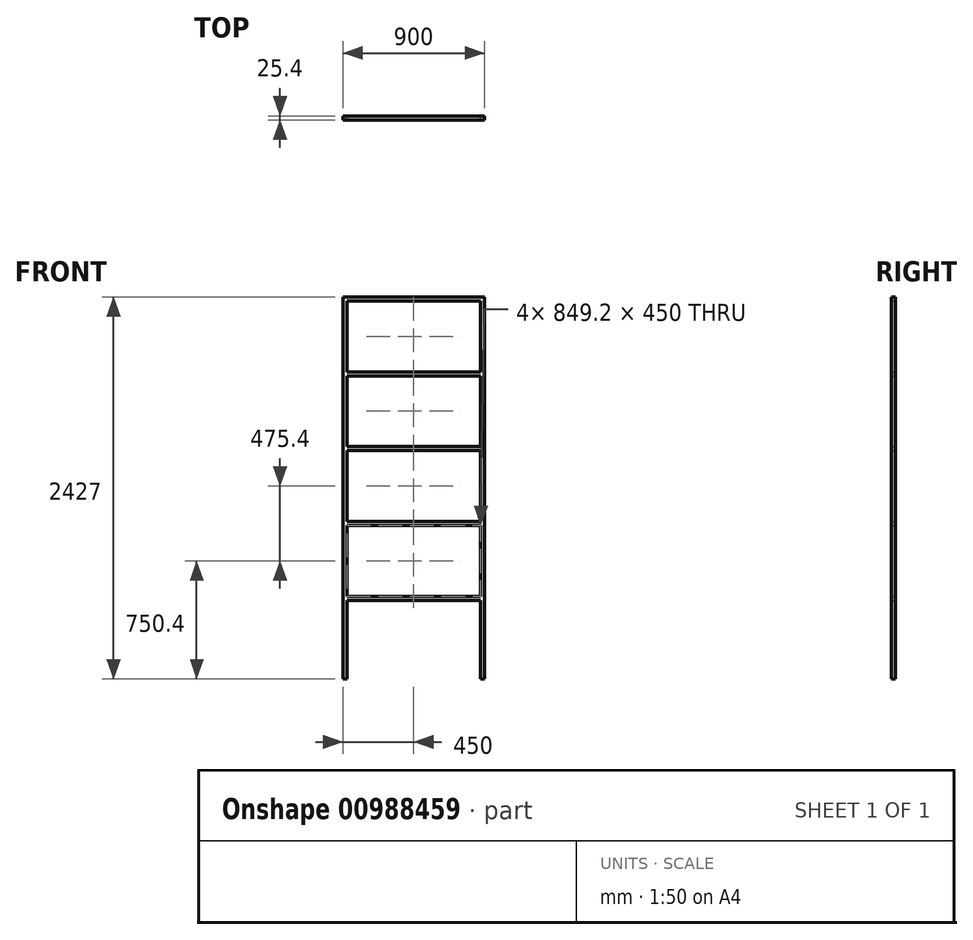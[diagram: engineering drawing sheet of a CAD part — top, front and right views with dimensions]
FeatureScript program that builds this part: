
annotation { "Feature Type Name" : "Feature", "Feature Type Description" : "" }
export const myFeature = defineFeature(function(context is Context, id is Id, definition is map)
    precondition{}
    {
        {
            var Q0;
            Q0=qCreatedBy(makeId("Front.planeOp"),FACE);
            var sketch = newSketch(context, id + "F0", { "sketchPlane" : qUnion([Q0])});
            skLineSegment(sketch, "E0", {"start": v(0, 0) * mm, "end": v(25.4, 0) * mm});
            skLineSegment(sketch, "E1", {"start": v(25.4, 0) * mm, "end": v(25.4, 500) * mm});
            skLineSegment(sketch, "E2", {"start": v(25.4, 500) * mm, "end": v(874.6, 500) * mm});
            skLineSegment(sketch, "E3", {"start": v(874.6, 500) * mm, "end": v(874.6, 0) * mm});
            skLineSegment(sketch, "E4", {"start": v(874.6, 0) * mm, "end": v(900, 0) * mm});
            skLineSegment(sketch, "E5", {"start": v(900, 0) * mm, "end": v(900, 2427) * mm});
            skLineSegment(sketch, "E6", {"start": v(25.4, 525.4) * mm, "end": v(874.6, 525.4) * mm});
            skLineSegment(sketch, "E7", {"start": v(25.4, 512.7) * mm, "end": v(874.6, 512.7) * mm, "construction": true});
            skLineSegment(sketch, "E8", {"start": v(25.4, 525.4) * mm, "end": v(25.4, 975.4) * mm});
            skLineSegment(sketch, "E9", {"start": v(874.6, 525.4) * mm, "end": v(874.6, 975.4) * mm});
            skLineSegment(sketch, "E10", {"start": v(874.6, 975.4) * mm, "end": v(25.4, 975.4) * mm});
            skLineSegment(sketch, "E11", {"start": v(25.4, 1000.8) * mm, "end": v(874.6, 1000.8) * mm});
            skLineSegment(sketch, "E12", {"start": v(25.4, 1000.8) * mm, "end": v(25.4, 1450.8) * mm});
            skLineSegment(sketch, "E13", {"start": v(25.4, 1450.8) * mm, "end": v(874.6, 1450.8) * mm});
            skLineSegment(sketch, "E14", {"start": v(874.6, 1450.8) * mm, "end": v(874.6, 1000.8) * mm});
            skLineSegment(sketch, "E15", {"start": v(25.4, 1476.2) * mm, "end": v(874.6, 1476.2) * mm});
            skLineSegment(sketch, "E16", {"start": v(25.4, 1476.2) * mm, "end": v(25.4, 1926.2) * mm});
            skLineSegment(sketch, "E17", {"start": v(25.4, 1926.2) * mm, "end": v(874.6, 1926.2) * mm});
            skLineSegment(sketch, "E18", {"start": v(874.6, 1926.2) * mm, "end": v(874.6, 1476.2) * mm});
            skLineSegment(sketch, "E19", {"start": v(0, 0) * mm, "end": v(0, 2427) * mm});
            skLineSegment(sketch, "E20", {"start": v(25.4, 1951.6) * mm, "end": v(874.6, 1951.6) * mm});
            skLineSegment(sketch, "E21", {"start": v(25.4, 1951.6) * mm, "end": v(25.4, 2401.6) * mm});
            skLineSegment(sketch, "E22", {"start": v(25.4, 2401.6) * mm, "end": v(874.6, 2401.6) * mm});
            skLineSegment(sketch, "E23", {"start": v(874.6, 2401.6) * mm, "end": v(874.6, 1951.6) * mm});
            skLineSegment(sketch, "E24", {"start": v(0, 2427) * mm, "end": v(900, 2427) * mm});
            skSolve(sketch);
        }
        {
            var Q0;
            Q0=makeQuery(id+"F0.imprint","IMPRINT",FACE,{"disambiguationData":[TD([[makeQuery(id+"F0.imprint","IMPRINT",EDGE,{"derivedFrom":sQuery(id+"F0.wireOp",EDGE,"E0")}),1.0]])]});
            extrude(context, id + "F1", {"entities" : qUnion([Q0]), "depth" : 25.4 * mm, "offsetDistance" : 25 * mm});
        }
    });
